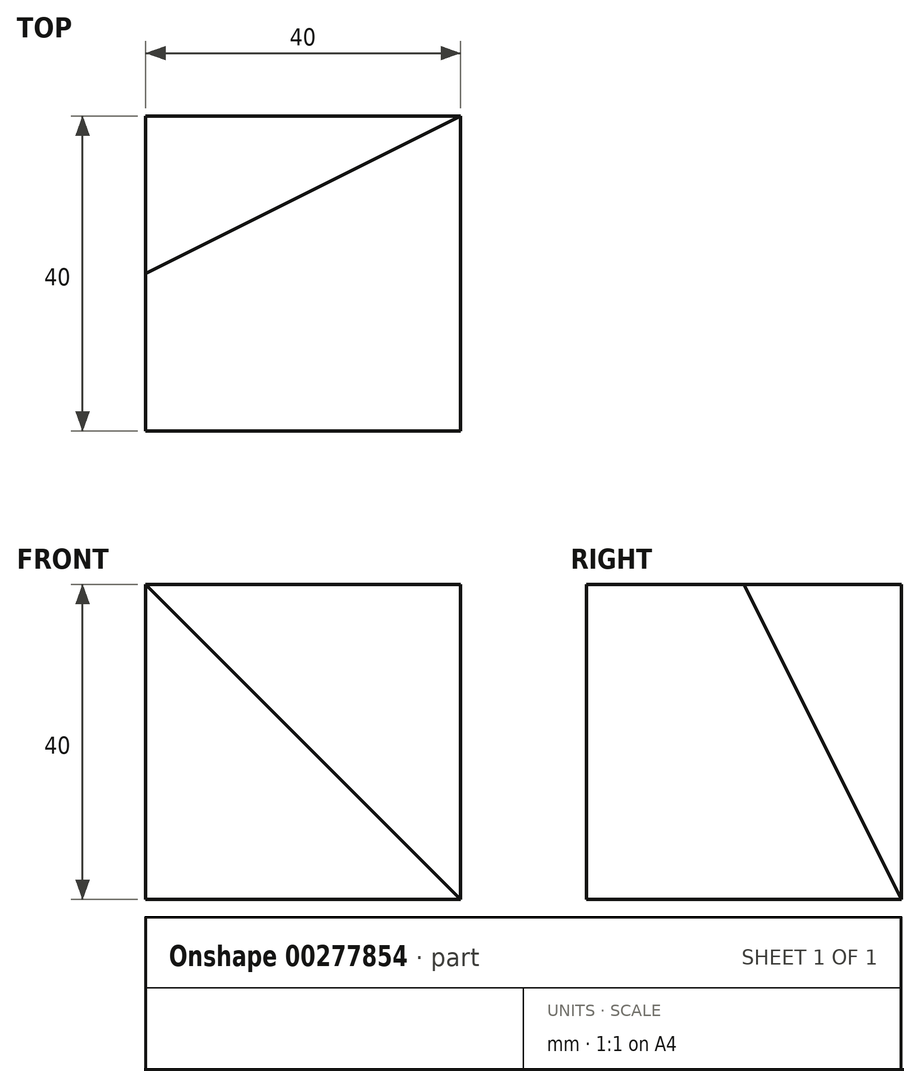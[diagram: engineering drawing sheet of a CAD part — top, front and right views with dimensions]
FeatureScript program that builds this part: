
annotation { "Feature Type Name" : "Feature", "Feature Type Description" : "" }
export const myFeature = defineFeature(function(context is Context, id is Id, definition is map)
    precondition{}
    {
        {
            var Q0;
            Q0=qCreatedBy(makeId("Front.planeOp"),FACE);
            var sketch = newSketch(context, id + "F0", { "sketchPlane" : qUnion([Q0])});
            skLineSegment(sketch, "E0.bottom", {"start": v(0, 0) * mm, "end": v(40, 0) * mm});
            skLineSegment(sketch, "E0.left", {"start": v(0, 0) * mm, "end": v(0, 40) * mm});
            skLineSegment(sketch, "E1", {"start": v(0, 40) * mm, "end": v(40, 0) * mm});
            skSolve(sketch);
        }
        {
            var Q0;
            Q0 = qSketchRegion(id + "F0", true);
            extrude(context, id + "F1", {"entities" : qUnion([Q0]), "depth" : 40 * mm});
        }
        {
            var Q0;
            Q0=makeQuery(id+"F1.opExtrude","SWEPT_FACE",FACE,{"disambiguationData":[OSD([sQuery(id+"F0.wireOp",EDGE,"E0.bottom")])]});
            var sketch = newSketch(context, id + "F2", { "sketchPlane" : qUnion([Q0])});
            skLineSegment(sketch, "E2", {"start": v(40, 0) * mm, "end": v(0, 20) * mm});
            skLineSegment(sketch, "E3.0", {"start": v(0, 20) * mm, "end": v(0, 0) * mm});
            skLineSegment(sketch, "E4.0", {"start": v(0, 0) * mm, "end": v(40, 0) * mm});
            skSolve(sketch);
        }
        {
            var Q0;
            Q0 = qSketchRegion(id + "F2", true);
            extrude(context, id + "F3", {"entities" : qUnion([Q0]), "operationType" : NewBodyOperationType.ADD, "oppositeDirection" : true, "depth" : 40 * mm});
        }
    });
